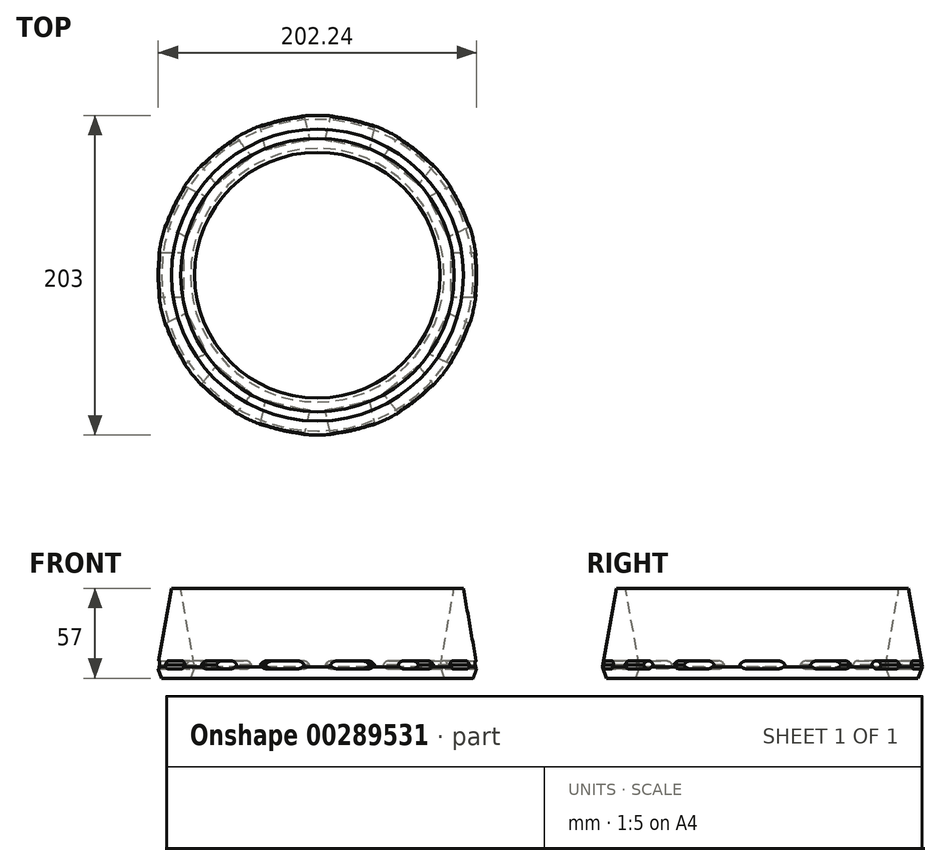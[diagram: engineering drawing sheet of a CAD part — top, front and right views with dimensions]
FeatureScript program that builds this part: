
annotation { "Feature Type Name" : "Feature", "Feature Type Description" : "" }
export const myFeature = defineFeature(function(context is Context, id is Id, definition is map)
    precondition{}
    {
        {
            var Q0;
            Q0=qCreatedBy(makeId("Front.planeOp"),FACE);
            var sketch = newSketch(context, id + "F0", { "sketchPlane" : qUnion([Q0])});
            skArc(sketch, "E0", {"start": v(85, 3.93) * mm, "mid": v(520, 18.95) * mm, "end": v(952.93, 63.93) * mm});
            skArc(sketch, "E1.0", {"start": v(85, -1.07) * mm, "mid": v(520.34, 13.96) * mm, "end": v(953.62, 58.98) * mm});
            skLineSegment(sketch, "E2", {"start": v(85, 3.93) * mm, "end": v(85, -1.07) * mm});
            skLineSegment(sketch, "E3", {"start": v(952.93, 63.93) * mm, "end": v(953.62, 58.98) * mm});
            skLineSegment(sketch, "E4", {"start": v(85, 3.93) * mm, "end": v(48.93, 3.93) * mm, "construction": true});
            skLineSegment(sketch, "E5", {"start": v(0, -9.83) * mm, "end": v(0, 243.77) * mm, "construction": true});
            skSolve(sketch);
        }
        {
            var Q0;
            Q0 = qSketchRegion(id + "F0", true);
            extrude(context, id + "F1", {"entities" : qUnion([Q0]), "depth" : 30 * mm, "symmetric" : true});
        }
        {
            var Q0;
            Q0=makeQuery(id+"F1.opExtrude","CAP_EDGE",EDGE,{"disambiguationData":[OSD([sQuery(id+"F0.wireOp",EDGE,"E0")])],"isStart":false});
            var Q1;
            Q1=makeQuery(id+"F1.opExtrude","CAP_EDGE",EDGE,{"disambiguationData":[OSD([sQuery(id+"F0.wireOp",EDGE,"E1.0")])],"isStart":false});
            var Q2;
            Q2=makeQuery(id+"F1.opExtrude","CAP_EDGE",EDGE,{"disambiguationData":[OSD([sQuery(id+"F0.wireOp",EDGE,"E0")])],"isStart":true});
            var Q3;
            Q3=makeQuery(id+"F1.opExtrude","CAP_EDGE",EDGE,{"disambiguationData":[OSD([sQuery(id+"F0.wireOp",EDGE,"E1.0")])],"isStart":true});
            fillet(context, id + "F2", {"entities" : qUnion([Q0, Q1, Q2, Q3]), "radius" : 5 * mm, "tangentPropagation" : true, "allowEdgeOverflow" : false});
        }
        {
            var Q0;
            Q0=makeQuery(id+"F1.opExtrude","SWEPT_BODY",BODY,{"disambiguationData":[OSD([sQuery(id+"F0.wireOp",EDGE,"E0"),sQuery(id+"F0.wireOp",EDGE,"E1.0"),sQuery(id+"F0.wireOp",EDGE,"E2"),sQuery(id+"F0.wireOp",EDGE,"E3")])]});
            var Q1;
            Q1=sQuery(id+"F0.wireOp",EDGE,"E5");
            circularPattern(context, id + "F3", {"entities" : qUnion([Q0]), "axis" : qUnion([Q1]), "angle" : 360 * degree, "instanceCount" : 14, "equalSpace" : true, "computeTransformsWithoutBuiltin" : true});
        }
        {
            var Q0;
            Q0=qCreatedBy(makeId("Top.planeOp"),FACE);
            var sketch = newSketch(context, id + "F4", { "sketchPlane" : qUnion([Q0])});
            skCircle(sketch, "E6", {"center": v(0, 0) * mm, "radius": 101.5 * mm});
            skCircle(sketch, "E7", {"center": v(0, 0) * mm, "radius": 78 * mm});
            skSolve(sketch);
        }
        {
            var Q0;
            Q0=makeQuery(id+"F4.imprint","IMPRINT",FACE,{"disambiguationData":[TD([[makeQuery(id+"F4.imprint","IMPRINT",EDGE,{"derivedFrom":sQuery(id+"F4.wireOp",EDGE,"E6")}),1.0]])]});
            var Q1;
            Q1=sQuery(id+"F4.wireOp",EDGE,"E6");
            extrude(context, id + "F5", {"entities" : qUnion([Q0]), "surfaceEntities" : qUnion([Q1]), "depth" : 50 * mm, "hasDraft" : true, "draftAngle" : 10 * degree, "draftPullDirection" : true, "hasSecondDirection" : true, "secondDirectionOppositeDirection" : true, "secondDirectionDepth" : 7 * mm, "hasSecondDirectionDraft" : true, "secondDirectionDraftAngle" : 20 * degree, "secondDirectionDraftPullDirection" : true});
        }
        {
            var Q0;
            Q0=makeQuery(id+"F1.opExtrude","SWEPT_BODY",BODY,{"disambiguationData":[OSD([sQuery(id+"F0.wireOp",EDGE,"E0"),sQuery(id+"F0.wireOp",EDGE,"E1.0"),sQuery(id+"F0.wireOp",EDGE,"E2"),sQuery(id+"F0.wireOp",EDGE,"E3")])]});
            var Q1;
            Q1=makeQuery(id+"F3.opPattern","COPY",BODY,{"derivedFrom":makeQuery(id+"F1.opExtrude","SWEPT_BODY",BODY,{"disambiguationData":[OSD([sQuery(id+"F0.wireOp",EDGE,"E0"),sQuery(id+"F0.wireOp",EDGE,"E1.0"),sQuery(id+"F0.wireOp",EDGE,"E2"),sQuery(id+"F0.wireOp",EDGE,"E3")])]}),"instanceName":"1"});
            var Q2;
            Q2=makeQuery(id+"F3.opPattern","COPY",BODY,{"derivedFrom":makeQuery(id+"F1.opExtrude","SWEPT_BODY",BODY,{"disambiguationData":[OSD([sQuery(id+"F0.wireOp",EDGE,"E0"),sQuery(id+"F0.wireOp",EDGE,"E1.0"),sQuery(id+"F0.wireOp",EDGE,"E2"),sQuery(id+"F0.wireOp",EDGE,"E3")])]}),"instanceName":"2"});
            var Q3;
            Q3=makeQuery(id+"F3.opPattern","COPY",BODY,{"derivedFrom":makeQuery(id+"F1.opExtrude","SWEPT_BODY",BODY,{"disambiguationData":[OSD([sQuery(id+"F0.wireOp",EDGE,"E0"),sQuery(id+"F0.wireOp",EDGE,"E1.0"),sQuery(id+"F0.wireOp",EDGE,"E2"),sQuery(id+"F0.wireOp",EDGE,"E3")])]}),"instanceName":"3"});
            var Q4;
            Q4=makeQuery(id+"F3.opPattern","COPY",BODY,{"derivedFrom":makeQuery(id+"F1.opExtrude","SWEPT_BODY",BODY,{"disambiguationData":[OSD([sQuery(id+"F0.wireOp",EDGE,"E0"),sQuery(id+"F0.wireOp",EDGE,"E1.0"),sQuery(id+"F0.wireOp",EDGE,"E2"),sQuery(id+"F0.wireOp",EDGE,"E3")])]}),"instanceName":"4"});
            var Q5;
            Q5=makeQuery(id+"F3.opPattern","COPY",BODY,{"derivedFrom":makeQuery(id+"F1.opExtrude","SWEPT_BODY",BODY,{"disambiguationData":[OSD([sQuery(id+"F0.wireOp",EDGE,"E0"),sQuery(id+"F0.wireOp",EDGE,"E1.0"),sQuery(id+"F0.wireOp",EDGE,"E2"),sQuery(id+"F0.wireOp",EDGE,"E3")])]}),"instanceName":"5"});
            var Q6;
            Q6=makeQuery(id+"F3.opPattern","COPY",BODY,{"derivedFrom":makeQuery(id+"F1.opExtrude","SWEPT_BODY",BODY,{"disambiguationData":[OSD([sQuery(id+"F0.wireOp",EDGE,"E0"),sQuery(id+"F0.wireOp",EDGE,"E1.0"),sQuery(id+"F0.wireOp",EDGE,"E2"),sQuery(id+"F0.wireOp",EDGE,"E3")])]}),"instanceName":"6"});
            var Q7;
            Q7=makeQuery(id+"F3.opPattern","COPY",BODY,{"derivedFrom":makeQuery(id+"F1.opExtrude","SWEPT_BODY",BODY,{"disambiguationData":[OSD([sQuery(id+"F0.wireOp",EDGE,"E0"),sQuery(id+"F0.wireOp",EDGE,"E1.0"),sQuery(id+"F0.wireOp",EDGE,"E2"),sQuery(id+"F0.wireOp",EDGE,"E3")])]}),"instanceName":"7"});
            var Q8;
            Q8=makeQuery(id+"F3.opPattern","COPY",BODY,{"derivedFrom":makeQuery(id+"F1.opExtrude","SWEPT_BODY",BODY,{"disambiguationData":[OSD([sQuery(id+"F0.wireOp",EDGE,"E0"),sQuery(id+"F0.wireOp",EDGE,"E1.0"),sQuery(id+"F0.wireOp",EDGE,"E2"),sQuery(id+"F0.wireOp",EDGE,"E3")])]}),"instanceName":"8"});
            var Q9;
            Q9=makeQuery(id+"F3.opPattern","COPY",BODY,{"derivedFrom":makeQuery(id+"F1.opExtrude","SWEPT_BODY",BODY,{"disambiguationData":[OSD([sQuery(id+"F0.wireOp",EDGE,"E0"),sQuery(id+"F0.wireOp",EDGE,"E1.0"),sQuery(id+"F0.wireOp",EDGE,"E2"),sQuery(id+"F0.wireOp",EDGE,"E3")])]}),"instanceName":"9"});
            var Q10;
            Q10=makeQuery(id+"F3.opPattern","COPY",BODY,{"derivedFrom":makeQuery(id+"F1.opExtrude","SWEPT_BODY",BODY,{"disambiguationData":[OSD([sQuery(id+"F0.wireOp",EDGE,"E0"),sQuery(id+"F0.wireOp",EDGE,"E1.0"),sQuery(id+"F0.wireOp",EDGE,"E2"),sQuery(id+"F0.wireOp",EDGE,"E3")])]}),"instanceName":"10"});
            var Q11;
            Q11=makeQuery(id+"F3.opPattern","COPY",BODY,{"derivedFrom":makeQuery(id+"F1.opExtrude","SWEPT_BODY",BODY,{"disambiguationData":[OSD([sQuery(id+"F0.wireOp",EDGE,"E0"),sQuery(id+"F0.wireOp",EDGE,"E1.0"),sQuery(id+"F0.wireOp",EDGE,"E2"),sQuery(id+"F0.wireOp",EDGE,"E3")])]}),"instanceName":"11"});
            var Q12;
            Q12=makeQuery(id+"F3.opPattern","COPY",BODY,{"derivedFrom":makeQuery(id+"F1.opExtrude","SWEPT_BODY",BODY,{"disambiguationData":[OSD([sQuery(id+"F0.wireOp",EDGE,"E0"),sQuery(id+"F0.wireOp",EDGE,"E1.0"),sQuery(id+"F0.wireOp",EDGE,"E2"),sQuery(id+"F0.wireOp",EDGE,"E3")])]}),"instanceName":"12"});
            var Q13;
            Q13=makeQuery(id+"F3.opPattern","COPY",BODY,{"derivedFrom":makeQuery(id+"F1.opExtrude","SWEPT_BODY",BODY,{"disambiguationData":[OSD([sQuery(id+"F0.wireOp",EDGE,"E0"),sQuery(id+"F0.wireOp",EDGE,"E1.0"),sQuery(id+"F0.wireOp",EDGE,"E2"),sQuery(id+"F0.wireOp",EDGE,"E3")])]}),"instanceName":"13"});
            var Q14;
            Q14=makeQuery(id+"F5.*.split.splitOp","SPLIT",BODY,{"derivedFrom":makeQuery(id+"F5.opExtrude","SWEPT_BODY",BODY,{"disambiguationData":[OSD([sQuery(id+"F4.wireOp",EDGE,"E6"),sQuery(id+"F4.wireOp",EDGE,"E7")])]})});
            booleanBodies(context, id + "F6", {"operationType" : BooleanOperationType.SUBTRACTION, "tools" : qUnion([Q0, Q1, Q2, Q3, Q4, Q5, Q6, Q7, Q8, Q9, Q10, Q11, Q12, Q13]), "targets" : qUnion([Q14])});
        }
    });
